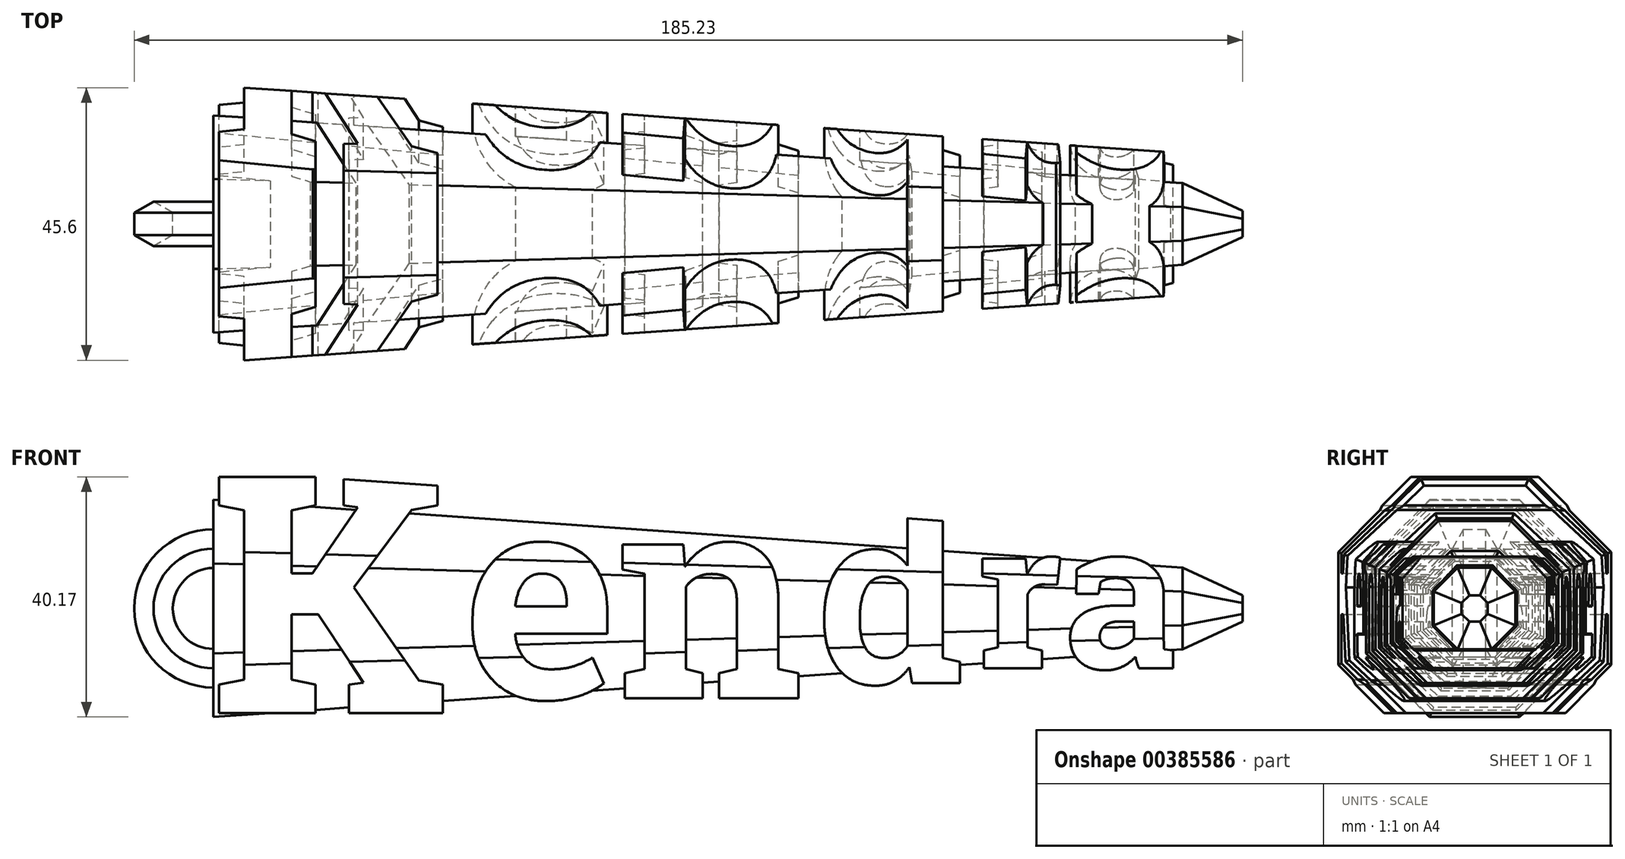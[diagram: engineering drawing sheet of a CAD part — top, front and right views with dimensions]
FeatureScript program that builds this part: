
annotation { "Feature Type Name" : "Feature", "Feature Type Description" : "" }
export const myFeature = defineFeature(function(context is Context, id is Id, definition is map)
    precondition{}
    {
        {
            assignVariable(context, id + "F0", {"name" : "hookPlane", "anyValue" : 81});
        }
        {
            assignVariable(context, id + "F1", {"name" : "halfLength", "anyValue" : 81});
        }
        {
            var Q0;
            Q0=qCreatedBy(makeId("Front.planeOp"),FACE);
            var sketch = newSketch(context, id + "F2", { "sketchPlane" : qUnion([Q0])});
            skText(sketch, "E0", { "text": "K", "fontName": "RobotoSlab-Bold.ttf"});
            skPoint(sketch, "E1", {"position": v(-39.27, 0) * mm});
            skText(sketch, "E2", { "text": "en", "fontName": "RobotoSlab-Bold.ttf"});
            skText(sketch, "E3", { "text": "d", "fontName": "RobotoSlab-Bold.ttf"});
            skText(sketch, "E4", { "text": "ra", "fontName": "RobotoSlab-Bold.ttf"});
            skPoint(sketch, "E5", {"position": v(19.74, 0) * mm});
            skPoint(sketch, "E6", {"position": v(46.34, 0) * mm});
            skLineSegment(sketch, "E7", {"start": v(-81.55, -20) * mm, "end": v(-81.55, -51.65) * mm, "construction": true});
            skLineSegment(sketch, "E8", {"start": v(-81.55, -51.65) * mm, "end": v(81.55, -51.65) * mm, "construction": true});
            skLineSegment(sketch, "E9", {"start": v(81.55, -51.65) * mm, "end": v(81.55, -12.5) * mm, "construction": true});
            skPoint(sketch, "E10", {"position": v(0, -51.65) * mm});
            const initialGuessF2  = {"E0": [-0.08155, -0.02, 1, 0, 0.04], "E2": [-0.03927, -0.0175, 1, 0, 0.035], "E3": [0.01974, -0.015, 1, 0, 0.03], "E4": [0.04634, -0.0125, 1, 0, 0.025]};
            skSetInitialGuess(sketch, initialGuessF2);
            skSolve(sketch);
        }
        {
            var Q0;
            Q0=qSketchRegion(id+"F2",true);
            extrude(context, id + "F3", {"entities" : qUnion([Q0]), "depth" : 25 * mm, "hasSecondDirection" : true, "secondDirectionOppositeDirection" : true, "secondDirectionDepth" : 25 * mm});
        }
        {
            var Q0;
            Q0=qCreatedBy(makeId("Right.planeOp"),FACE);
            var sketch = newSketch(context, id + "F4", { "sketchPlane" : qUnion([Q0])});
            skCircle(sketch, "E11", {"center": v(0, -2.5) * mm, "radius": 12.5 * mm, "construction": true});
            skLineSegment(sketch, "E12", {"start": v(0, 14.75) * mm, "end": v(0, 9.1) * mm, "construction": true});
            skLineSegment(sketch, "E13.0", {"start": v(-5.18, 10) * mm, "end": v(5.18, 10) * mm});
            skLineSegment(sketch, "E13.1", {"start": v(5.18, 10) * mm, "end": v(12.5, 2.67) * mm});
            skLineSegment(sketch, "E13.2", {"start": v(12.5, 2.67) * mm, "end": v(12.5, -7.68) * mm});
            skLineSegment(sketch, "E13.3", {"start": v(12.5, -7.68) * mm, "end": v(5.18, -15) * mm});
            skLineSegment(sketch, "E13.4", {"start": v(5.18, -15) * mm, "end": v(-5.18, -15) * mm});
            skLineSegment(sketch, "E13.5", {"start": v(-5.18, -15) * mm, "end": v(-12.5, -7.68) * mm});
            skLineSegment(sketch, "E13.6", {"start": v(-12.5, -7.68) * mm, "end": v(-12.5, 2.67) * mm});
            skLineSegment(sketch, "E13.7", {"start": v(-12.5, 2.67) * mm, "end": v(-5.18, 10) * mm});
            skPoint(sketch, "E13.0.midPoint", {"position": v(0, 10) * mm});
            skLineSegment(sketch, "E14", {"start": v(0, 19.5) * mm, "end": v(0, 10) * mm});
            skSolve(sketch);
        }
        {
            var Q0;
            Q0=qSketchRegion(id+"F4",true);
            var Q1;
            Q1=makeQuery(id+"F3.opExtrude","SWEPT_FACE",FACE,{"disambiguationData":[OSD([sQuery(id+"F2.wireOp",EDGE,"E4.sketch_text.stroke-1")])]});
            extrude(context, id + "F5", {"entities" : qUnion([Q0]), "operationType" : NewBodyOperationType.ADD, "oppositeDirection" : true, "depth" : (getVariable(context, 'halfLength')) * mm, "hasDraft" : true, "draftAngle" : 4 * degree, "hasSecondDirection" : true, "secondDirectionOppositeDirection" : false, "secondDirectionBoundEntityFace" : qUnion([Q1]), "secondDirectionDepth" : (getVariable(context, 'halfLength')) * mm, "hasSecondDirectionDraft" : true, "secondDirectionDraftAngle" : 4 * degree, "secondDirectionDraftPullDirection" : true});
        }
        {
            var Q0;
            Q0=qCreatedBy(makeId("Right.planeOp"),FACE);
            var sketch = newSketch(context, id + "F6", { "sketchPlane" : qUnion([Q0])});
            skCircle(sketch, "E15.cCircle", {"center": v(0, -2.5) * mm, "radius": 17.5 * mm, "construction": true});
            skLineSegment(sketch, "E15.0", {"start": v(-7.25, 15) * mm, "end": v(7.25, 15) * mm});
            skLineSegment(sketch, "E15.1", {"start": v(7.25, 15) * mm, "end": v(17.5, 4.75) * mm});
            skLineSegment(sketch, "E15.2", {"start": v(17.5, 4.75) * mm, "end": v(17.5, -9.75) * mm});
            skLineSegment(sketch, "E15.3", {"start": v(17.5, -9.75) * mm, "end": v(7.25, -20) * mm});
            skLineSegment(sketch, "E15.4", {"start": v(7.25, -20) * mm, "end": v(-7.25, -20) * mm});
            skLineSegment(sketch, "E15.5", {"start": v(-7.25, -20) * mm, "end": v(-17.5, -9.75) * mm});
            skLineSegment(sketch, "E15.6", {"start": v(-17.5, -9.75) * mm, "end": v(-17.5, 4.75) * mm});
            skLineSegment(sketch, "E15.7", {"start": v(-17.5, 4.75) * mm, "end": v(-7.25, 15) * mm});
            skLineSegment(sketch, "E16.bottom", {"start": v(37.5, 35) * mm, "end": v(-37.5, 35) * mm});
            skLineSegment(sketch, "E16.top", {"start": v(37.5, -40) * mm, "end": v(-37.5, -40) * mm});
            skLineSegment(sketch, "E16.left", {"start": v(37.5, 35) * mm, "end": v(37.5, -40) * mm});
            skLineSegment(sketch, "E16.right", {"start": v(-37.5, 35) * mm, "end": v(-37.5, -40) * mm});
            skLineSegment(sketch, "E17", {"start": v(0, 19.5) * mm, "end": v(0, -8.52) * mm, "construction": true});
            skSolve(sketch);
        }
        {
            var Q0;
            Q0=makeQuery(id+"F6.imprint","IMPRINT",FACE,{"disambiguationData":[TD([[makeQuery(id+"F6.imprint","IMPRINT",EDGE,{"derivedFrom":sQuery(id+"F6.wireOp",EDGE,"E15.0")}),1.0]])]});
            extrude(context, id + "F7", {"entities" : qUnion([Q0]), "operationType" : NewBodyOperationType.REMOVE, "endBound" : BoundingType.THROUGH_ALL, "depth" : 25 * mm, "hasDraft" : true, "draftAngle" : 4 * degree, "hasSecondDirection" : true, "secondDirectionBound" : SecondDirectionBoundingType.THROUGH_ALL, "secondDirectionOppositeDirection" : true, "secondDirectionDepth" : 25 * mm, "hasSecondDirectionDraft" : true, "secondDirectionDraftAngle" : 4 * degree, "secondDirectionDraftPullDirection" : true});
        }
        {
            var Q0;
            {var subQ0=sQuery(id+"F4.wireOp",EDGE,"E13.3");var subQ1=sQuery(id+"F4.wireOp",EDGE,"E13.2");var subQ2=sQuery(id+"F4.wireOp",EDGE,"E13.4");var subQ3=sQuery(id+"F4.wireOp",EDGE,"E13.5");var subQ4=sQuery(id+"F4.wireOp",EDGE,"E13.6");Q0=makeQuery(id+"F5.boolean.opBoolean","SPLIT",FACE,{"disambiguationData":[TD([makeQuery(id+"F3.opExtrude","SWEPT_FACE",FACE,{"disambiguationData":[OSD([sQuery(id+"F2.wireOp",EDGE,"E4.sketch_text.stroke-0")])]})])],"derivedFrom":makeQuery(id+"F5.opExtrude","CAP_FACE",FACE,{"disambiguationData":[OSD([sQuery(id+"F4.wireOp",EDGE,"E13.0"),sQuery(id+"F4.wireOp",EDGE,"E13.1"),subQ1,subQ0,subQ2,subQ3,subQ4,sQuery(id+"F4.wireOp",EDGE,"E13.7")])],"isStart":true})});}
            var sketch = newSketch(context, id + "F8", { "sketchPlane" : qUnion([Q0])});
            skCircle(sketch, "E18.cCircle", {"center": v(0, -2.5) * mm, "radius": 6.84 * mm, "construction": true});
            skLineSegment(sketch, "E18.0", {"start": v(-2.83, 4.33) * mm, "end": v(2.83, 4.33) * mm});
            skLineSegment(sketch, "E18.1", {"start": v(2.83, 4.33) * mm, "end": v(6.84, 0.33) * mm});
            skLineSegment(sketch, "E18.2", {"start": v(6.84, 0.33) * mm, "end": v(6.84, -5.34) * mm});
            skLineSegment(sketch, "E18.3", {"start": v(6.84, -5.34) * mm, "end": v(2.83, -9.34) * mm});
            skLineSegment(sketch, "E18.4", {"start": v(2.83, -9.34) * mm, "end": v(-2.83, -9.34) * mm});
            skLineSegment(sketch, "E18.5", {"start": v(-2.83, -9.34) * mm, "end": v(-6.84, -5.34) * mm});
            skLineSegment(sketch, "E18.6", {"start": v(-6.84, -5.34) * mm, "end": v(-6.84, 0.33) * mm});
            skLineSegment(sketch, "E18.7", {"start": v(-6.84, 0.33) * mm, "end": v(-2.83, 4.33) * mm});
            skPoint(sketch, "E18.0.midPoint", {"position": v(0, 4.33) * mm});
            skLineSegment(sketch, "E19", {"start": v(0, 19.59) * mm, "end": v(0, -20.57) * mm, "construction": true});
            skSolve(sketch);
        }
        {
            var Q0;
            Q0=qSketchRegion(id+"F8",true);
            extrude(context, id + "F9", {"entities" : qUnion([Q0]), "operationType" : NewBodyOperationType.ADD, "depth" : 10 * mm, "hasDraft" : true, "draftAngle" : 25 * degree, "draftPullDirection" : true});
        }
        {
            var Q0;
            Q0=qCreatedBy(makeId("Right.planeOp"),FACE);
            cPlane(context, id + "F10", {"entities" : qUnion([Q0]), "cplaneType" : CPlaneType.OFFSET, "offset" : (getVariable(context, 'hookPlane')) * mm, "oppositeDirection" : true, "width" : 150 * mm, "height" : 150 * mm});
        }
        {
            var Q0;
            Q0=qCreatedBy(makeId("Front.planeOp"),FACE);
            var sketch = newSketch(context, id + "F11", { "sketchPlane" : qUnion([Q0])});
            skArc(sketch, "E20", {"start": v(-74.39, 5) * mm, "mid": v(-91, -2.5) * mm, "end": v(-74.39, -10) * mm});
            skLineSegment(sketch, "E21", {"start": v(-74.39, 5) * mm, "end": v(-74.39, -10) * mm, "construction": true});
            skPoint(sketch, "E22", {"position": v(-74.39, -2.5) * mm});
            skLineSegment(sketch, "E23", {"start": v(-81, 15.66) * mm, "end": v(-81, -20.67) * mm, "construction": true});
            skSolve(sketch);
        }
        {
            var Q0;
            Q0=qCreatedBy(id+"F10.planeOp",FACE);
            var sketch = newSketch(context, id + "F12", { "sketchPlane" : qUnion([Q0])});
            skCircle(sketch, "E24.cCircle", {"center": v(0, 7.5) * mm, "radius": 3.23 * mm, "construction": true});
            skLineSegment(sketch, "E24.0", {"start": v(1.87, 4.26) * mm, "end": v(-1.87, 4.26) * mm});
            skLineSegment(sketch, "E24.1", {"start": v(-1.87, 4.26) * mm, "end": v(-3.73, 7.5) * mm});
            skLineSegment(sketch, "E24.2", {"start": v(-3.73, 7.5) * mm, "end": v(-1.87, 10.73) * mm});
            skLineSegment(sketch, "E24.3", {"start": v(-1.87, 10.73) * mm, "end": v(1.87, 10.73) * mm});
            skLineSegment(sketch, "E24.4", {"start": v(1.87, 10.73) * mm, "end": v(3.73, 7.5) * mm});
            skLineSegment(sketch, "E24.5", {"start": v(3.73, 7.5) * mm, "end": v(1.87, 4.26) * mm});
            skPoint(sketch, "E24.0.midPoint", {"position": v(0, 4.26) * mm});
            skSolve(sketch);
        }
        {
            var Q0;
            Q0=qSketchRegion(id+"F12",true);
            var Q1;
            Q1=qConstructionFilter(qBodyType(qCreatedBy(id+"F11",EDGE),BodyType.WIRE),ConstructionObject.NO);
            sweep(context, id + "F13", {"operationType" : NewBodyOperationType.ADD, "profiles" : qUnion([Q0]), "path" : qUnion([Q1])});
        }
    });
